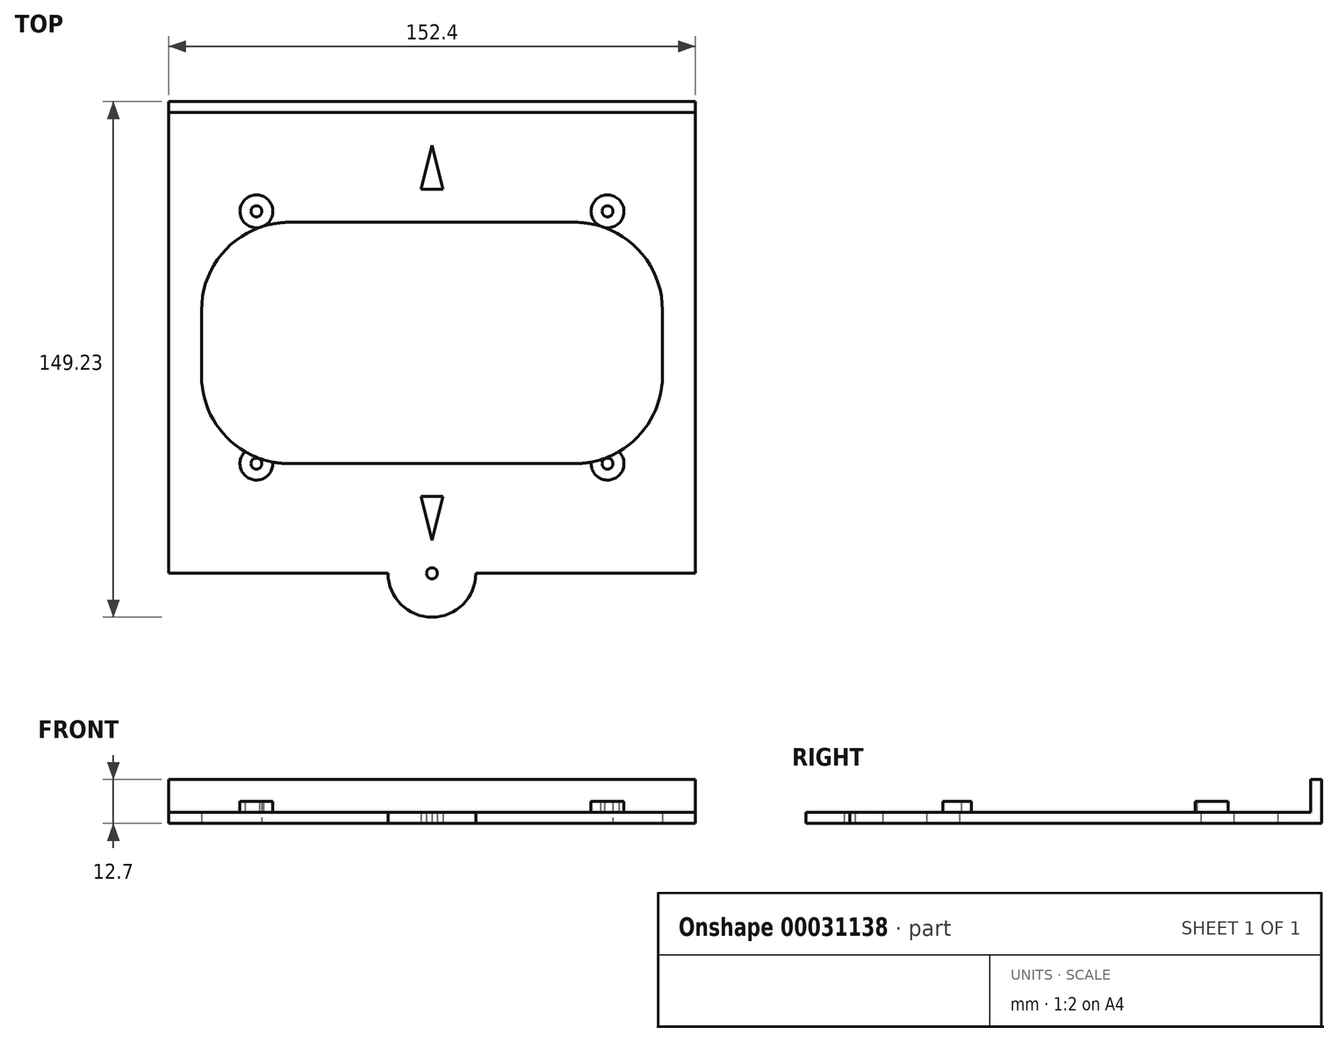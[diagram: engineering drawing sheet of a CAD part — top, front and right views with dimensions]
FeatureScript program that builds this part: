
annotation { "Feature Type Name" : "Feature", "Feature Type Description" : "" }
export const myFeature = defineFeature(function(context is Context, id is Id, definition is map)
    precondition{}
    {
        {
            var Q0;
            Q0=qCreatedBy(makeId("Top.planeOp"),FACE);
            var sketch = newSketch(context, id + "F0", { "sketchPlane" : qUnion([Q0])});
            skLineSegment(sketch, "E0.rect.top", {"start": v(76.2, 63.5) * mm, "end": v(-76.2, 63.5) * mm});
            skLineSegment(sketch, "E0.rect.left", {"start": v(76.2, -63.5) * mm, "end": v(76.2, 63.5) * mm});
            skLineSegment(sketch, "E0.rect.right", {"start": v(-76.2, -63.5) * mm, "end": v(-76.2, 63.5) * mm});
            skPoint(sketch, "E0.rect.middle", {"position": v(0, 0) * mm});
            skLineSegment(sketch, "E1", {"start": v(-76.2, 60.32) * mm, "end": v(76.2, 60.33) * mm});
            skPoint(sketch, "E2", {"position": v(0, 60.33) * mm});
            skPoint(sketch, "E3.start.orphan", {"position": v(0, 38.1) * mm});
            skCircle(sketch, "E4", {"center": v(0, -73.03) * mm, "radius": 1.59 * mm});
            skLineSegment(sketch, "E5", {"start": v(-76.2, -63.5) * mm, "end": v(-76.2, -73.03) * mm});
            skLineSegment(sketch, "E6", {"start": v(-76.2, -73.03) * mm, "end": v(-12.7, -73.03) * mm});
            skLineSegment(sketch, "E7", {"start": v(76.2, -73.03) * mm, "end": v(76.2, -63.5) * mm});
            skLineSegment(sketch, "E8.trimOffspring", {"start": v(12.7, -73.03) * mm, "end": v(76.2, -73.03) * mm});
            skLineSegment(sketch, "E9", {"start": v(0, -63.5) * mm, "end": v(3.17, -50.8) * mm});
            skLineSegment(sketch, "E10", {"start": v(3.17, -50.8) * mm, "end": v(-3.18, -50.8) * mm});
            skLineSegment(sketch, "E11", {"start": v(-3.18, -50.8) * mm, "end": v(0, -63.5) * mm});
            skPoint(sketch, "E12.end.orphan", {"position": v(0, -50.8) * mm});
            skPoint(sketch, "E13.end.orphan", {"position": v(0, 57.15) * mm});
            skPoint(sketch, "E14.orphan", {"position": v(3.17, 38.1) * mm});
            skPoint(sketch, "E15.end.orphan", {"position": v(-3.18, 38.1) * mm});
            skLineSegment(sketch, "E16", {"start": v(0, 50.8) * mm, "end": v(-3.18, 38.1) * mm});
            skLineSegment(sketch, "E17", {"start": v(3.17, 38.1) * mm, "end": v(0, 50.8) * mm});
            skLineSegment(sketch, "E18", {"start": v(-3.18, 38.1) * mm, "end": v(3.17, 38.1) * mm});
            skCircle(sketch, "E19", {"center": v(-50.8, 31.75) * mm, "radius": 1.59 * mm});
            skCircle(sketch, "E20", {"center": v(-50.8, 31.75) * mm, "radius": 4.76 * mm});
            skCircle(sketch, "E21", {"center": v(50.8, 31.75) * mm, "radius": 1.59 * mm});
            skCircle(sketch, "E22", {"center": v(50.8, 31.75) * mm, "radius": 4.76 * mm});
            skCircle(sketch, "E23", {"center": v(50.8, -41.28) * mm, "radius": 1.59 * mm});
            skCircle(sketch, "E24", {"center": v(50.8, -41.28) * mm, "radius": 4.76 * mm});
            skCircle(sketch, "E25", {"center": v(-50.8, -41.28) * mm, "radius": 1.59 * mm});
            skCircle(sketch, "E26", {"center": v(-50.8, -41.28) * mm, "radius": 4.76 * mm});
            skArc(sketch, "E27.trimOffspring", {"start": v(-12.7, -73.03) * mm, "mid": v(0, -85.73) * mm, "end": v(12.7, -73.03) * mm});
            skPoint(sketch, "E28.center.orphan", {"position": v(0, -79.38) * mm});
            skLineSegment(sketch, "E29.rect.bottom", {"start": v(41.28, -41.27) * mm, "end": v(-41.28, -41.27) * mm});
            skLineSegment(sketch, "E29.rect.top", {"start": v(41.28, 28.58) * mm, "end": v(-41.28, 28.58) * mm});
            skLineSegment(sketch, "E29.rect.left", {"start": v(66.68, -15.87) * mm, "end": v(66.68, 3.18) * mm});
            skLineSegment(sketch, "E29.rect.right", {"start": v(-66.68, -15.87) * mm, "end": v(-66.68, 3.18) * mm});
            skPoint(sketch, "E29.rect.middle", {"position": v(0, -6.35) * mm});
            skPoint(sketch, "E30.visualSharp", {"position": v(-66.68, -41.27) * mm});
            skArc(sketch, "E30.filletArc", {"start": v(-66.68, -15.87) * mm, "mid": v(-59.24, -33.84) * mm, "end": v(-41.28, -41.27) * mm});
            skPoint(sketch, "E31.visualSharp", {"position": v(-66.68, 28.58) * mm});
            skArc(sketch, "E31.filletArc", {"start": v(-41.28, 28.58) * mm, "mid": v(-59.24, 21.14) * mm, "end": v(-66.68, 3.18) * mm});
            skPoint(sketch, "E32.visualSharp", {"position": v(66.68, 28.58) * mm});
            skArc(sketch, "E32.filletArc", {"start": v(66.68, 3.18) * mm, "mid": v(59.24, 21.14) * mm, "end": v(41.28, 28.58) * mm});
            skPoint(sketch, "E33.visualSharp", {"position": v(66.68, -41.27) * mm});
            skArc(sketch, "E33.filletArc", {"start": v(41.28, -41.27) * mm, "mid": v(59.24, -33.84) * mm, "end": v(66.67, -15.87) * mm});
            skSolve(sketch);
        }
        {
            var Q0;
            Q0=makeQuery(id+"F0.imprint","IMPRINT",FACE,{"disambiguationData":[TD([[makeQuery(id+"F0.imprint","IMPRINT",EDGE,{"derivedFrom":sQuery(id+"F0.wireOp",EDGE,"aa0e41e1-5804-4a8c-9730-617fea006d48")}),-1.0]])]});
            var Q1;
            {var subQ1=sQuery(id+"F0.wireOp",EDGE,"E1");Q1=makeQuery(id+"F0.imprint","IMPRINT",FACE,{"disambiguationData":[TD([[makeQuery(id+"F0.imprint","IMPRINT",EDGE,{"derivedFrom":subQ1}),-1.0]])]});}
            var Q2;
            {var subQ2=sQuery(id+"F0.wireOp",EDGE,"E0.rect.top");Q2=makeQuery(id+"F0.imprint","IMPRINT",FACE,{"disambiguationData":[TD([[makeQuery(id+"F0.imprint","IMPRINT",EDGE,{"derivedFrom":subQ2}),1.0]])]});}
            var Q3;
            Q3=makeQuery(id+"F0.imprint","IMPRINT",FACE,{"disambiguationData":[TD([[makeQuery(id+"F0.imprint","IMPRINT",EDGE,{"derivedFrom":sQuery(id+"F0.wireOp",EDGE,"E19")}),-1.0]])]});
            var Q4;
            Q4=makeQuery(id+"F0.imprint","IMPRINT",FACE,{"disambiguationData":[TD([[makeQuery(id+"F0.imprint","IMPRINT",EDGE,{"derivedFrom":sQuery(id+"F0.wireOp",EDGE,"E21")}),-1.0]])]});
            var Q5;
            Q5=makeQuery(id+"F0.imprint","IMPRINT",FACE,{"disambiguationData":[TD([[makeQuery(id+"F0.imprint","IMPRINT",EDGE,{"derivedFrom":sQuery(id+"F0.wireOp",EDGE,"E23")}),-1.0]])]});
            var Q6;
            Q6=makeQuery(id+"F0.imprint","IMPRINT",FACE,{"disambiguationData":[TD([[makeQuery(id+"F0.imprint","IMPRINT",EDGE,{"derivedFrom":sQuery(id+"F0.wireOp",EDGE,"E25")}),-1.0]])]});
            var Q7;
            Q7=makeQuery(id+"F0.imprint","IMPRINT",FACE,{"disambiguationData":[TD([[makeQuery(id+"F0.imprint","IMPRINT",EDGE,{"derivedFrom":sQuery(id+"F0.wireOp",EDGE,"042c20f7-fe0c-4b33-a80c-553bca925f40")}),-1.0]])]});
            var Q8;
            Q8=makeQuery(id+"F0.imprint","IMPRINT",FACE,{"disambiguationData":[TD([[makeQuery(id+"F0.imprint","IMPRINT",EDGE,{"derivedFrom":sQuery(id+"F0.wireOp",EDGE,"2c958d5a-7b25-4786-83a1-58e83ce19abd")}),-1.0]])]});
            extrude(context, id + "F1", {"entities" : qUnion([Q0, Q1, Q2, Q3, Q4, Q5, Q6, Q7, Q8]), "depth" : 3.17 * mm});
        }
        {
            var Q0;
            Q0=makeQuery(id+"F0.imprint","IMPRINT",FACE,{"disambiguationData":[TD([[makeQuery(id+"F0.imprint","IMPRINT",EDGE,{"derivedFrom":sQuery(id+"F0.wireOp",EDGE,"aa0e41e1-5804-4a8c-9730-617fea006d48")}),-1.0]])]});
            var Q1;
            Q1=makeQuery(id+"F0.imprint","IMPRINT",FACE,{"disambiguationData":[TD([[makeQuery(id+"F0.imprint","IMPRINT",EDGE,{"derivedFrom":sQuery(id+"F0.wireOp",EDGE,"E25")}),-1.0]])]});
            var Q2;
            Q2=makeQuery(id+"F0.imprint","IMPRINT",FACE,{"disambiguationData":[TD([[makeQuery(id+"F0.imprint","IMPRINT",EDGE,{"derivedFrom":sQuery(id+"F0.wireOp",EDGE,"E19")}),-1.0]])]});
            var Q3;
            Q3=makeQuery(id+"F0.imprint","IMPRINT",FACE,{"disambiguationData":[TD([[makeQuery(id+"F0.imprint","IMPRINT",EDGE,{"derivedFrom":sQuery(id+"F0.wireOp",EDGE,"E23")}),-1.0]])]});
            var Q4;
            Q4=makeQuery(id+"F0.imprint","IMPRINT",FACE,{"disambiguationData":[TD([[makeQuery(id+"F0.imprint","IMPRINT",EDGE,{"derivedFrom":sQuery(id+"F0.wireOp",EDGE,"E21")}),-1.0]])]});
            var Q5;
            Q5=makeQuery(id+"F0.imprint","IMPRINT",FACE,{"disambiguationData":[TD([[makeQuery(id+"F0.imprint","IMPRINT",EDGE,{"derivedFrom":sQuery(id+"F0.wireOp",EDGE,"2c958d5a-7b25-4786-83a1-58e83ce19abd")}),-1.0]])]});
            extrude(context, id + "F2", {"entities" : qUnion([Q0, Q1, Q2, Q3, Q4, Q5]), "operationType" : NewBodyOperationType.ADD, "depth" : 6.35 * mm});
        }
        {
            var Q0;
            {var subQ2=sQuery(id+"F0.wireOp",EDGE,"E0.rect.top");Q0=makeQuery(id+"F0.imprint","IMPRINT",FACE,{"disambiguationData":[TD([[makeQuery(id+"F0.imprint","IMPRINT",EDGE,{"derivedFrom":subQ2}),1.0]])]});}
            extrude(context, id + "F3", {"entities" : qUnion([Q0]), "operationType" : NewBodyOperationType.ADD, "depth" : 12.7 * mm});
        }
    });
